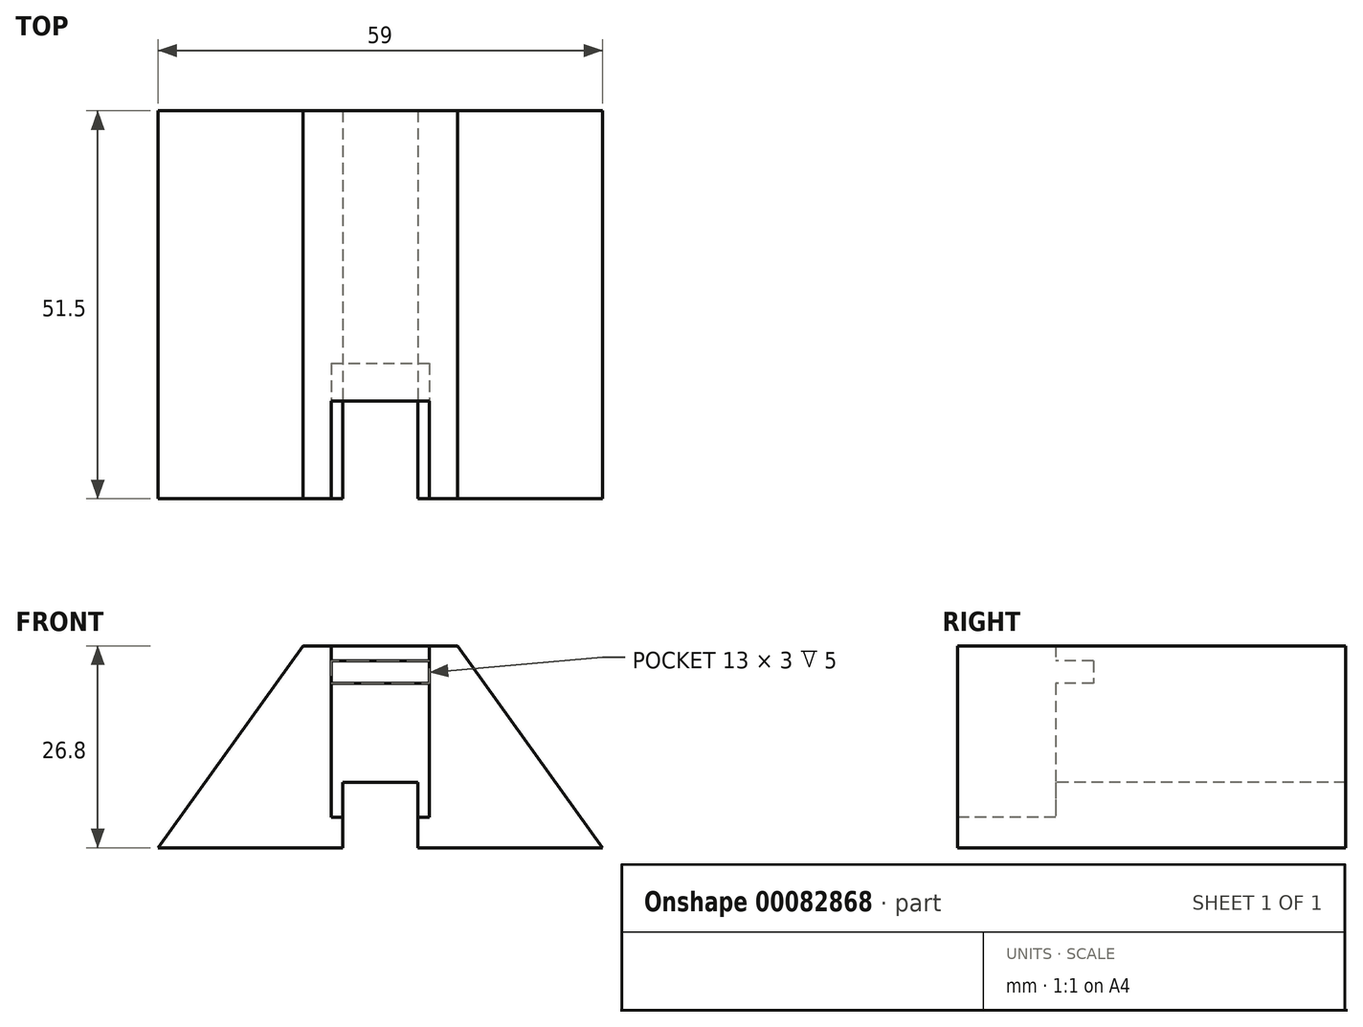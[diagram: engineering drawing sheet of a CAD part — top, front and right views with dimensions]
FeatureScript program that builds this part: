
annotation { "Feature Type Name" : "Feature", "Feature Type Description" : "" }
export const myFeature = defineFeature(function(context is Context, id is Id, definition is map)
    precondition{}
    {
        {
            var Q0;
            Q0=qCreatedBy(makeId("Top.planeOp"),FACE);
            var sketch = newSketch(context, id + "F0", { "sketchPlane" : qUnion([Q0])});
            skLineSegment(sketch, "E0.bottom", {"start": v(-29.5, 25.75) * mm, "end": v(29.5, 25.75) * mm});
            skLineSegment(sketch, "E0.top", {"start": v(-29.5, -25.75) * mm, "end": v(29.5, -25.75) * mm});
            skLineSegment(sketch, "E0.left", {"start": v(-29.5, 25.75) * mm, "end": v(-29.5, -25.75) * mm});
            skLineSegment(sketch, "E0.right", {"start": v(29.5, 25.75) * mm, "end": v(29.5, -25.75) * mm});
            skSolve(sketch);
        }
        {
            var Q0;
            Q0=makeQuery(id+"F0.imprint","IMPRINT",FACE,{"disambiguationData":[TD([[makeQuery(id+"F0.imprint","IMPRINT",EDGE,{"derivedFrom":sQuery(id+"F0.wireOp",EDGE,"E0.bottom")}),-1.0]])]});
            extrude(context, id + "F1", {"entities" : qUnion([Q0]), "depth" : 26.8 * mm});
        }
        {
            var Q0;
            Q0=makeQuery(id+"F1.opExtrude","SWEPT_FACE",FACE,{"disambiguationData":[OSD([sQuery(id+"F0.wireOp",EDGE,"E0.top")])]});
            var sketch = newSketch(context, id + "F2", { "sketchPlane" : qUnion([Q0])});
            skLineSegment(sketch, "E1", {"start": v(-29.5, 0) * mm, "end": v(-10.24, 26.8) * mm});
            skLineSegment(sketch, "E2", {"start": v(29.5, 0) * mm, "end": v(10.24, 26.8) * mm});
            skSolve(sketch);
        }
        {
            var Q0;
            {var subQ0=sQuery(id+"F2.wireOp",EDGE,"E1");Q0=makeQuery(id+"F2.imprint","IMPRINT",FACE,{"disambiguationData":[TD([[makeQuery(id+"F2.imprint","IMPRINT",EDGE,{"derivedFrom":subQ0}),1.0]])]});}
            var Q1;
            {var subQ0=sQuery(id+"F2.wireOp",EDGE,"E2");Q1=makeQuery(id+"F2.imprint","IMPRINT",FACE,{"disambiguationData":[TD([[makeQuery(id+"F2.imprint","IMPRINT",EDGE,{"derivedFrom":subQ0}),-1.0]])]});}
            extrude(context, id + "F3", {"entities" : qUnion([Q0, Q1]), "operationType" : NewBodyOperationType.REMOVE, "oppositeDirection" : true, "depth" : 55 * mm});
        }
        {
            var Q0;
            Q0=makeQuery(id+"F1.opExtrude","SWEPT_FACE",FACE,{"disambiguationData":[OSD([sQuery(id+"F0.wireOp",EDGE,"E0.top")])]});
            var sketch = newSketch(context, id + "F4", { "sketchPlane" : qUnion([Q0])});
            skLineSegment(sketch, "E3.bottom", {"start": v(-5, 8.67) * mm, "end": v(5, 8.67) * mm});
            skLineSegment(sketch, "E3.top", {"start": v(-5, 0) * mm, "end": v(5, 0) * mm});
            skLineSegment(sketch, "E3.left", {"start": v(-5, 8.67) * mm, "end": v(-5, 0) * mm});
            skLineSegment(sketch, "E3.right", {"start": v(5, 8.67) * mm, "end": v(5, 0) * mm});
            skSolve(sketch);
        }
        {
            var Q0;
            Q0=qSketchRegion(id+"F4",true);
            extrude(context, id + "F5", {"entities" : qUnion([Q0]), "operationType" : NewBodyOperationType.REMOVE, "endBound" : BoundingType.THROUGH_ALL, "oppositeDirection" : true, "depth" : 25 * mm});
        }
        {
            var Q0;
            Q0=makeQuery(id+"F1.opExtrude","SWEPT_FACE",FACE,{"disambiguationData":[OSD([sQuery(id+"F0.wireOp",EDGE,"E0.top")])]});
            var sketch = newSketch(context, id + "F6", { "sketchPlane" : qUnion([Q0])});
            skLineSegment(sketch, "E4.bottom", {"start": v(-6.5, 26.8) * mm, "end": v(6.5, 26.8) * mm});
            skLineSegment(sketch, "E4.top", {"start": v(-6.5, 4.05) * mm, "end": v(6.5, 4.05) * mm});
            skLineSegment(sketch, "E4.left", {"start": v(-6.5, 26.8) * mm, "end": v(-6.5, 4.05) * mm});
            skLineSegment(sketch, "E4.right", {"start": v(6.5, 26.8) * mm, "end": v(6.5, 4.05) * mm});
            skSolve(sketch);
        }
        {
            var Q0;
            Q0=makeQuery(id+"F6.imprint","IMPRINT",FACE,{"disambiguationData":[TD([[makeQuery(id+"F6.imprint","IMPRINT",EDGE,{"derivedFrom":sQuery(id+"F6.wireOp",EDGE,"E4.bottom")}),-1.0]])]});
            extrude(context, id + "F7", {"entities" : qUnion([Q0]), "operationType" : NewBodyOperationType.REMOVE, "oppositeDirection" : true, "depth" : 13 * mm});
        }
        {
            var Q0;
            Q0=makeQuery(id+"F7.boolean.opBoolean","COPY",FACE,{"derivedFrom":makeQuery(id+"F7.opExtrude","CAP_FACE",FACE,{"disambiguationData":[OSD([sQuery(id+"F4.wireOp",EDGE,"E3.bottom"),sQuery(id+"F4.wireOp",EDGE,"E3.left"),sQuery(id+"F4.wireOp",EDGE,"E3.right"),sQuery(id+"F6.wireOp",EDGE,"E4.bottom"),sQuery(id+"F6.wireOp",EDGE,"E4.top"),sQuery(id+"F6.wireOp",EDGE,"E4.left"),sQuery(id+"F6.wireOp",EDGE,"E4.right")])],"isStart":false})});
            var sketch = newSketch(context, id + "F8", { "sketchPlane" : qUnion([Q0])});
            skLineSegment(sketch, "E5.bottom", {"start": v(-6.5, 24.8) * mm, "end": v(6.5, 24.8) * mm});
            skLineSegment(sketch, "E5.top", {"start": v(-6.5, 21.8) * mm, "end": v(6.5, 21.8) * mm});
            skLineSegment(sketch, "E5.left", {"start": v(-6.5, 24.8) * mm, "end": v(-6.5, 21.8) * mm});
            skLineSegment(sketch, "E5.right", {"start": v(6.5, 24.8) * mm, "end": v(6.5, 21.8) * mm});
            skSolve(sketch);
        }
        {
            var Q0;
            Q0=qSketchRegion(id+"F8",true);
            extrude(context, id + "F9", {"entities" : qUnion([Q0]), "operationType" : NewBodyOperationType.REMOVE, "oppositeDirection" : true, "depth" : 5 * mm});
        }
    });
